# Revit family: L-school 16 Premium
name_source: partatom
category: Осветительные приборы
revit_build: Autodesk Revit 2017 (Build: 20160225_1515(x64)
units: mm (PartAtom-declared; Revit-internal decimal feet)

## family parameters
Источник света = Да
Общий = Нет
Основа = Грань
При загрузке вырезать с полостями = Нет
Размер круглого соединителя = Использовать диаметр
Тип детали = Нормальный
Точка расчета площади = Нет

## types (2) — shared parameters
Видимая форма излучения при визуализации = Нет
Излучение по длине прямоугольника = 594 мм
Излучение по ширине прямоугольника = 197 мм
Классификация нагрузок = Освещение
Комментарии к типоразмеру = Для образовательных учреждений
Кривая сил света = Д
Описание = Светильник L-school 16 Premium предназначен для установки в школах, больницах, и других общественных помещениях (офисы, кабинеты, торговые залы).
Отметка по умолчанию = 1219 мм
Полная установленная мощность = 15 В·А
Расстояние от светильника до поверхности = 56 мм
Световой поток светильника = 1750 лм
Светофильтр = 16777215
Смещение цветовой температуры при затухании лампы = <Нет>
Тип корпуса = L-school 16_body
Угол наклона = 90.00°

## per-type parameters (varying)
| type | Артикул | Изготовитель | Файл фотометрической сетки | Цветовая температура |
| L-school 16 Premium 4.0K | 111003 |  | L-school 16-15-D-4.0K-02-Premium.ies | 4000 K |
| L-school 16 Premium 5.0K | 111002 | LEDEL | L-school 16-15-D-5.0K-02-Premium.ies | 5000 K |

## geometry (parser evidence)
native form markers: Sweep x2
no freeform markers — native parametric forms only
